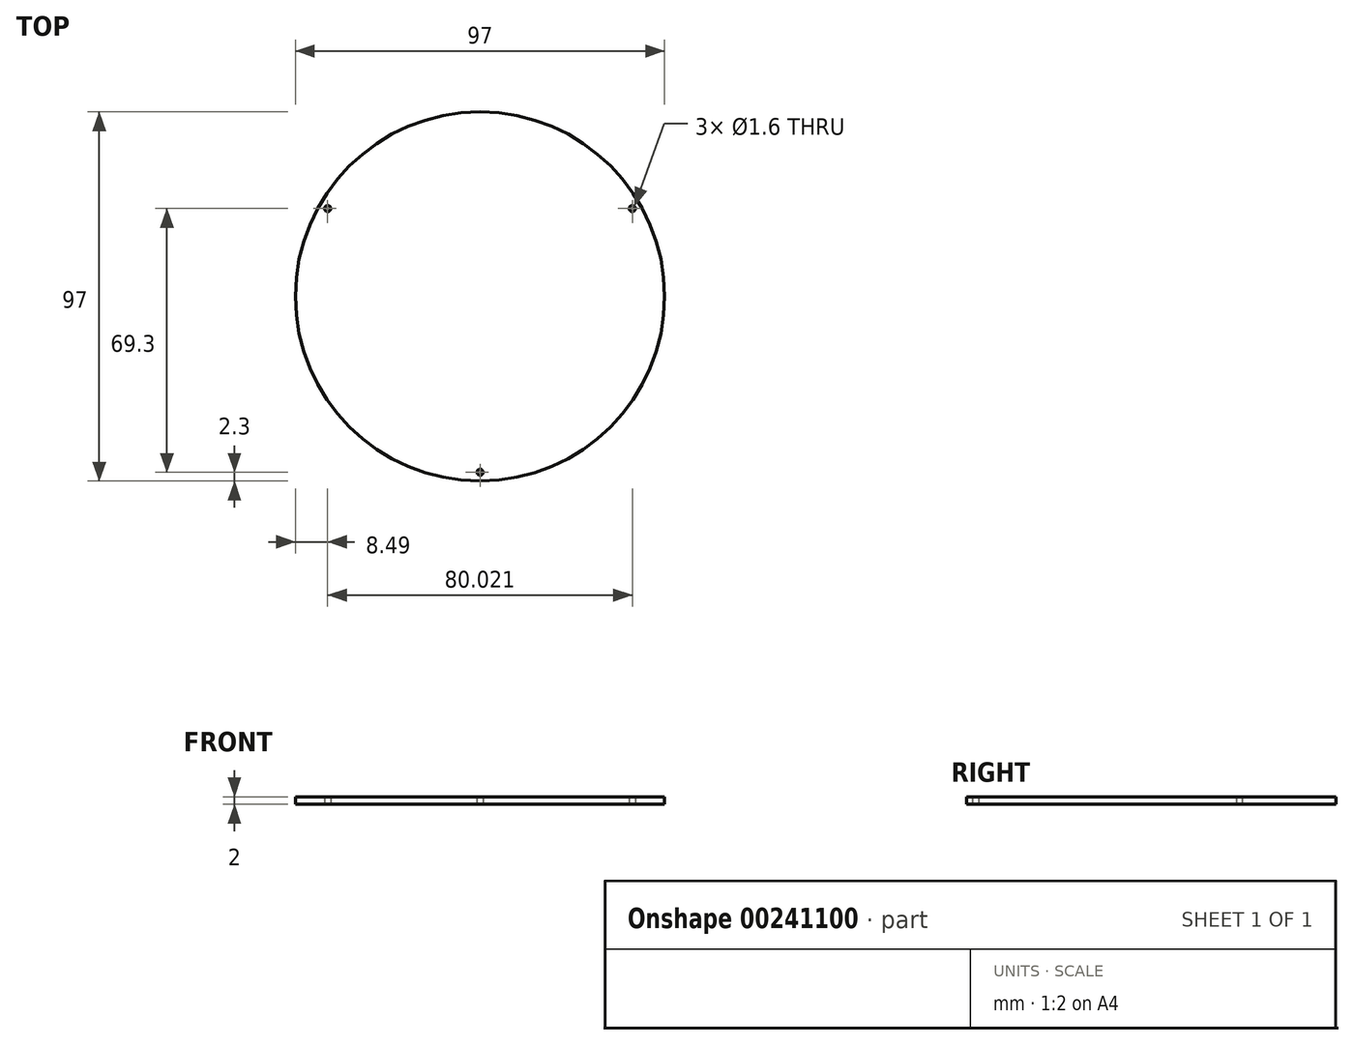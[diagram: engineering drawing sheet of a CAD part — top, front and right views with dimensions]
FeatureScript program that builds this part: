
annotation { "Feature Type Name" : "Feature", "Feature Type Description" : "" }
export const myFeature = defineFeature(function(context is Context, id is Id, definition is map)
    precondition{}
    {
        {
            var Q0;
            Q0=qCreatedBy(makeId("Top.planeOp"),FACE);
            var sketch = newSketch(context, id + "F0", { "sketchPlane" : qUnion([Q0])});
            skPoint(sketch, "E0.center", {"position": v(0, 0) * mm});
            skCircle(sketch, "E1", {"center": v(0, -46.2) * mm, "radius": 0.8 * mm});
            skCircle(sketch, "E2.1.0", {"center": v(40.01, 23.1) * mm, "radius": 0.8 * mm});
            skCircle(sketch, "E2.2.0", {"center": v(-40.01, 23.1) * mm, "radius": 0.8 * mm});
            skCircle(sketch, "E3", {"center": v(0, 0) * mm, "radius": 48.5 * mm});
            skSolve(sketch);
        }
        {
            var Q0;
            Q0 = qSketchRegion(id + "F0", true);
            extrude(context, id + "F1", {"entities" : qUnion([Q0]), "depth" : 2 * mm});
        }
    });
